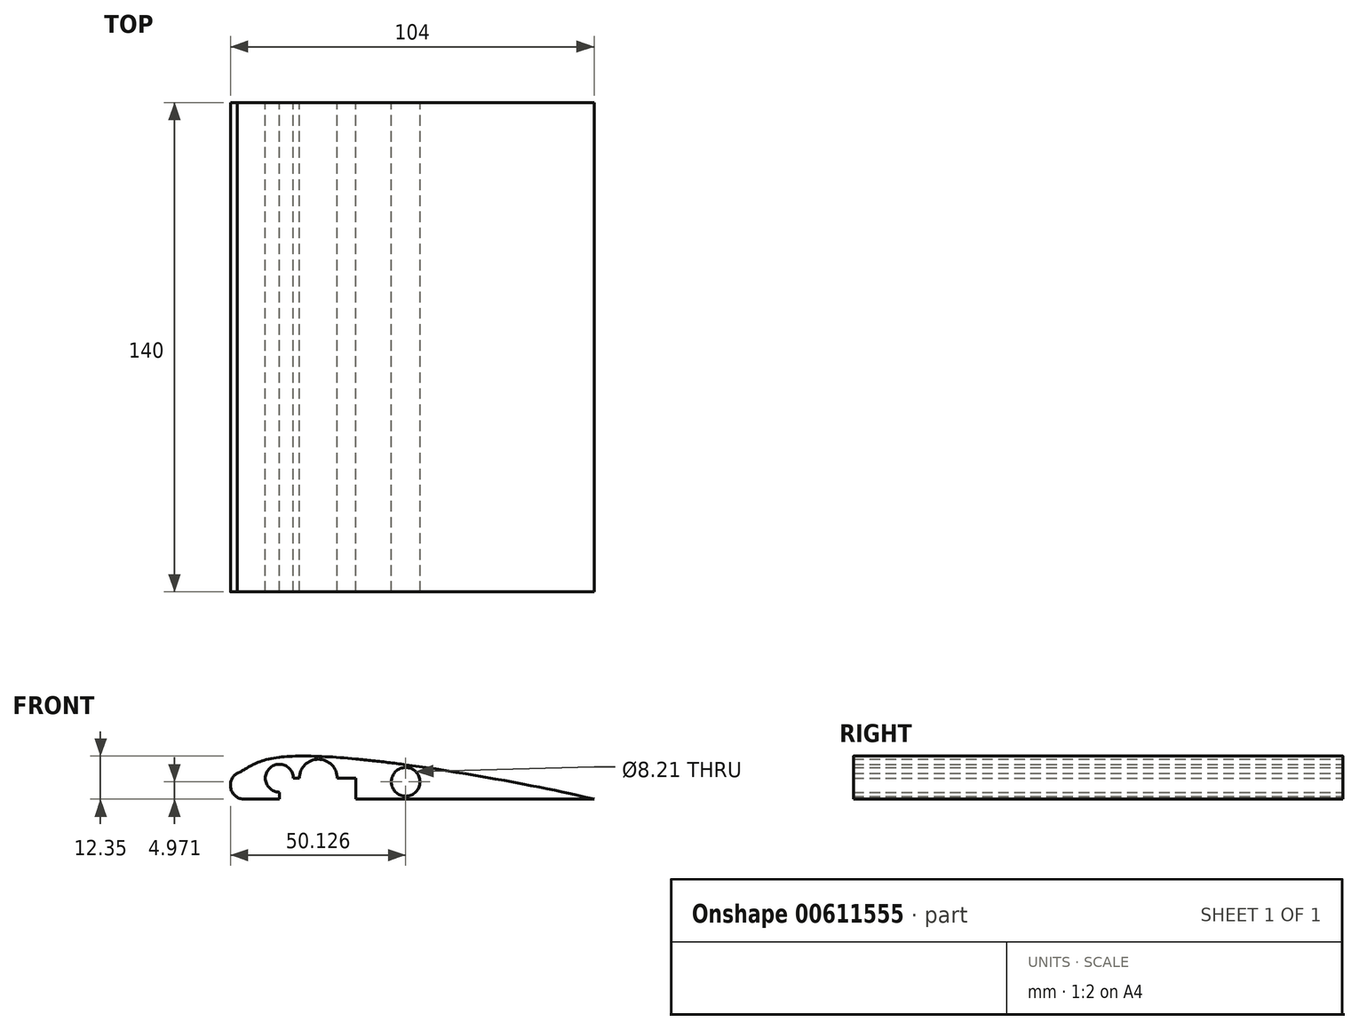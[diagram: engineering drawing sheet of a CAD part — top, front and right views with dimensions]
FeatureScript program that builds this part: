
annotation { "Feature Type Name" : "Feature", "Feature Type Description" : "" }
export const myFeature = defineFeature(function(context is Context, id is Id, definition is map)
    precondition{}
    {
        {
            var Q0;
            Q0=qCreatedBy(makeId("Front.planeOp"),FACE);
            var sketch = newSketch(context, id + "F0", { "sketchPlane" : qUnion([Q0])});
            skLineSegment(sketch, "E0", {"start": v(8.9, -4) * mm, "end": v(18.9, -4) * mm});
            skLineSegment(sketch, "E1", {"start": v(18.9, -4) * mm, "end": v(44.5, -4) * mm});
            skLineSegment(sketch, "E2", {"start": v(8.9, -4) * mm, "end": v(8.9, 4) * mm});
            skLineSegment(sketch, "E3", {"start": v(18.9, -4) * mm, "end": v(18.9, 8) * mm});
            skLineSegment(sketch, "E4", {"start": v(8.9, -4) * mm, "end": v(8.9, 0) * mm});
            skArc(sketch, "E5", {"start": v(8.9, -4) * mm, "mid": v(5.04, -1.04) * mm, "end": v(6.9, 3.46) * mm});
            skFitSpline(sketch, "E6", {"points": [v(6.9, 3.46) * mm, v(18.9, 8) * mm, v(108.9, -4) * mm], "startDerivative": vector(25.72, 9) * mm, "endDerivative": vector(55.93, -14.48) * mm});
            skLineSegment(sketch, "E7", {"start": v(44.5, -4) * mm, "end": v(108.9, -4) * mm});
            skLineSegment(sketch, "E8", {"start": v(44.5, -4) * mm, "end": v(40.83, -4) * mm});
            skLineSegment(sketch, "E9", {"start": v(40.83, -4) * mm, "end": v(40.83, 7.52) * mm});
            skCircle(sketch, "E10", {"center": v(8.9, 0) * mm, "radius": 4 * mm});
            skLineSegment(sketch, "E11", {"start": v(18.9, -4) * mm, "end": v(18.9, 2) * mm});
            skCircle(sketch, "E12", {"center": v(18.9, 2) * mm, "radius": 4 * mm});
            skLineSegment(sketch, "E13.right", {"start": v(55.04, 10.81) * mm, "end": v(55.04, -6.12) * mm});
            skLineSegment(sketch, "E14", {"start": v(18.9, 2) * mm, "end": v(30.05, 2) * mm});
            skLineSegment(sketch, "E15", {"start": v(30.05, 2) * mm, "end": v(40.83, 2) * mm});
            skLineSegment(sketch, "E16", {"start": v(40.83, 2) * mm, "end": v(55.04, 0.97) * mm});
            skCircle(sketch, "E17", {"center": v(30.05, 2) * mm, "radius": 5.42 * mm});
            skCircle(sketch, "E18", {"center": v(55.04, 0.97) * mm, "radius": 4.1 * mm});
            skSolve(sketch);
        }
        {
            var Q0;
            {var subQ0=sQuery(id+"F0.wireOp",EDGE,"E2");Q0=makeQuery(id+"F0.imprint","IMPRINT",FACE,{"disambiguationData":[TD([[makeQuery(id+"F0.imprint","IMPRINT",EDGE,{"derivedFrom":subQ0}),-1.0]])]});}
            var Q1;
            {var subQ1=sQuery(id+"F0.wireOp",EDGE,"E2");Q1=makeQuery(id+"F0.imprint","IMPRINT",FACE,{"disambiguationData":[TD([[makeQuery(id+"F0.imprint","IMPRINT",EDGE,{"derivedFrom":subQ1}),1.0]])]});}
            var Q2;
            {var subQ8=sQuery(id+"F0.wireOp",EDGE,"E0");Q2=makeQuery(id+"F0.imprint","IMPRINT",FACE,{"disambiguationData":[TD([[makeQuery(id+"F0.imprint","IMPRINT",EDGE,{"derivedFrom":subQ8}),1.0]])]});}
            var Q3;
            {var subQ1=sQuery(id+"F0.wireOp",EDGE,"E1");Q3=makeQuery(id+"F0.imprint","IMPRINT",FACE,{"disambiguationData":[TD([[makeQuery(id+"F0.imprint","IMPRINT",EDGE,{"derivedFrom":subQ1}),1.0]])]});}
            var Q4;
            {var subQ0=sQuery(id+"F0.wireOp",EDGE,"E7");Q4=makeQuery(id+"F0.imprint","IMPRINT",FACE,{"disambiguationData":[TD([[makeQuery(id+"F0.imprint","IMPRINT",EDGE,{"derivedFrom":subQ0}),1.0]])]});}
            var Q5;
            {var subQ1=sQuery(id+"F0.wireOp",EDGE,"E3");var subQ10=sQuery(id+"F0.wireOp",EDGE,"E6");var subQ12=makeQuery(id+"F0.imprint","INTERSECT",VERTEX,{"derivedFrom":[subQ1,subQ10]});Q5=makeQuery(id+"F0.imprint","IMPRINT",FACE,{"disambiguationData":[TD([[makeQuery(id+"F0.imprint","IMPRINT",EDGE,{"disambiguationData":[TD([[subQ12,1.0]])],"derivedFrom":subQ1}),-1.0]])]});}
            var Q6;
            {var subQ1=sQuery(id+"F0.wireOp",EDGE,"E6");var subQ5=sQuery(id+"F0.wireOp",EDGE,"E9");var subQ6=makeQuery(id+"F0.imprint","INTERSECT",VERTEX,{"derivedFrom":[subQ1,subQ5]});Q6=makeQuery(id+"F0.imprint","IMPRINT",FACE,{"disambiguationData":[TD([[makeQuery(id+"F0.imprint","IMPRINT",EDGE,{"disambiguationData":[TD([[subQ6,-1.0]])],"derivedFrom":subQ1}),-1.0]])]});}
            var Q7;
            {var subQ1=sQuery(id+"F0.wireOp",EDGE,"E8");Q7=makeQuery(id+"F0.imprint","IMPRINT",FACE,{"disambiguationData":[TD([[makeQuery(id+"F0.imprint","IMPRINT",EDGE,{"derivedFrom":subQ1}),-1.0]])]});}
            extrude(context, id + "F1", {"entities" : qUnion([Q0, Q1, Q2, Q3, Q4, Q5, Q6, Q7]), "depth" : 140 * mm, "offsetDistance" : 25 * mm});
        }
    });
